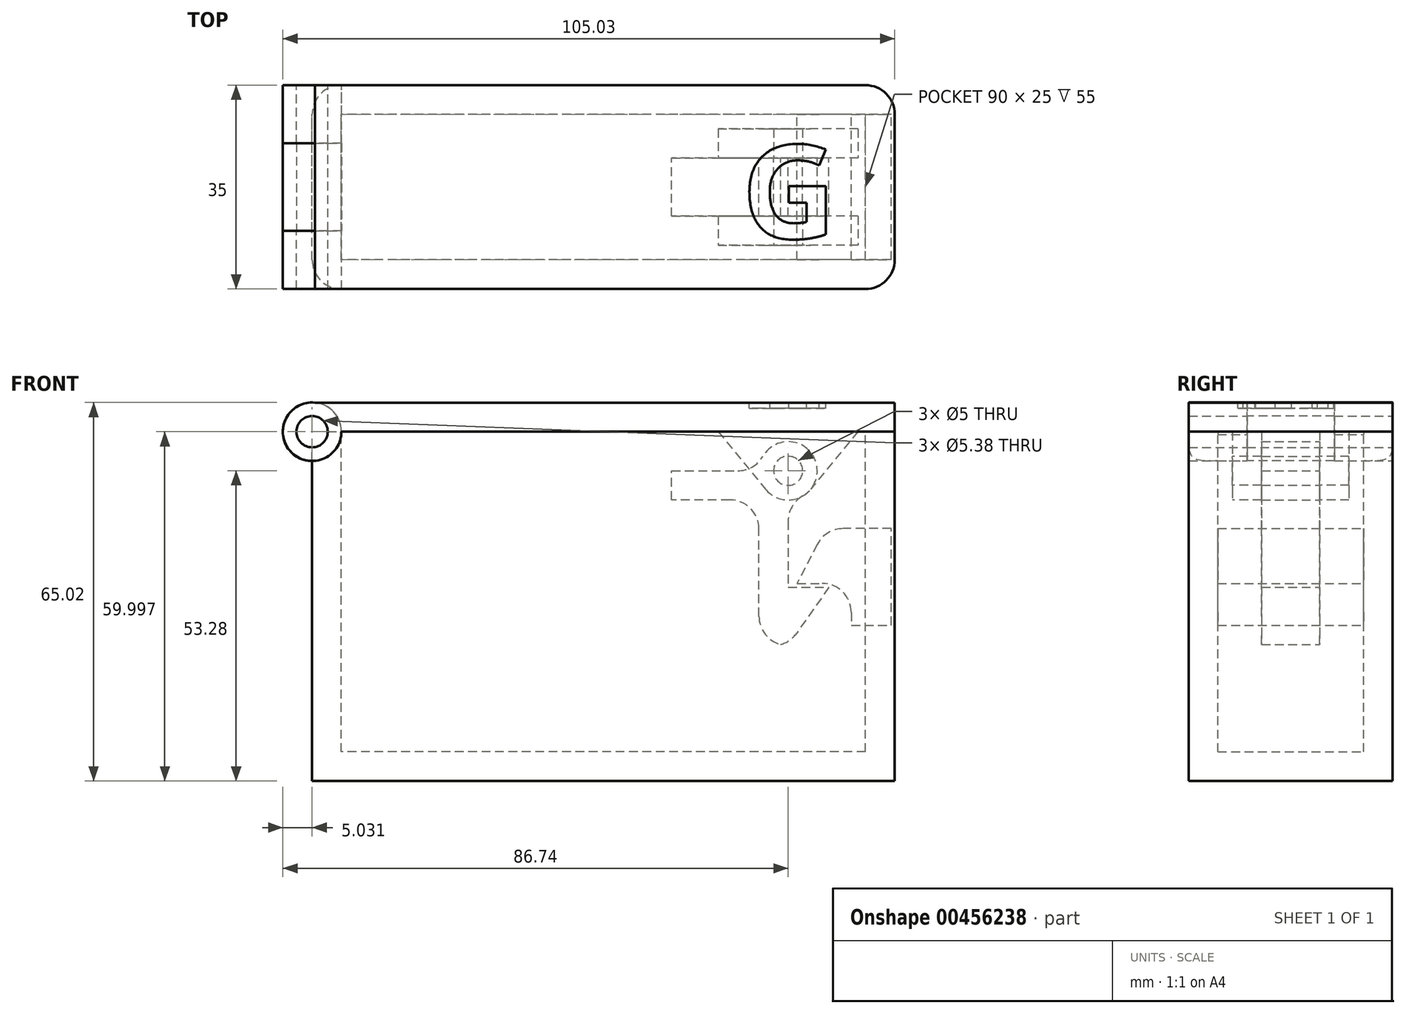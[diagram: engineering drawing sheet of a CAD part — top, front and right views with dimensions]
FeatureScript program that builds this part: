
annotation { "Feature Type Name" : "Feature", "Feature Type Description" : "" }
export const myFeature = defineFeature(function(context is Context, id is Id, definition is map)
    precondition{}
    {
        {
            var Q0;
            Q0=qCreatedBy(makeId("Front.planeOp"),FACE);
            var sketch = newSketch(context, id + "F0", { "sketchPlane" : qUnion([Q0])});
            skLineSegment(sketch, "E0", {"start": v(0, -30) * mm, "end": v(-5, -30) * mm});
            skLineSegment(sketch, "E1", {"start": v(-5, -30) * mm, "end": v(-5, -5) * mm});
            skLineSegment(sketch, "E2", {"start": v(-5, -5) * mm, "end": v(-20, -5) * mm});
            skLineSegment(sketch, "E3", {"start": v(-20, -5) * mm, "end": v(-20, 0) * mm});
            skLineSegment(sketch, "E4", {"start": v(-20, 0) * mm, "end": v(-5, 0) * mm});
            skLineSegment(sketch, "E5", {"start": v(0, -20) * mm, "end": v(7, -20) * mm});
            skLineSegment(sketch, "E6", {"start": v(7, -20) * mm, "end": v(0, -30) * mm});
            skArc(sketch, "E7", {"start": v(0, -5) * mm, "mid": v(3.54, 3.54) * mm, "end": v(-5, 0) * mm});
            skCircle(sketch, "E8", {"center": v(0, 0) * mm, "radius": 2.5 * mm});
            skLineSegment(sketch, "E9.trimOffspring", {"start": v(0, -5) * mm, "end": v(0, -20) * mm});
            skSolve(sketch);
        }
        {
            var Q0;
            Q0=makeQuery(id+"F0.imprint","IMPRINT",FACE,{"disambiguationData":[TD([[makeQuery(id+"F0.imprint","IMPRINT",EDGE,{"derivedFrom":sQuery(id+"F0.wireOp",EDGE,"E0")}),-1.0]])]});
            extrude(context, id + "F1", {"entities" : qUnion([Q0]), "endBound" : BoundingType.SYMMETRIC, "depth" : 10 * mm});
        }
        {
            var Q0;
            Q0=makeQuery(id+"F1.opExtrude","SWEPT_EDGE",EDGE,{"disambiguationData":[OSD([sQuery(id+"F0.wireOp",EDGE,"E1"),sQuery(id+"F0.wireOp",EDGE,"E2")])]});
            var Q1;
            Q1=makeQuery(id+"F1.opExtrude","SWEPT_EDGE",EDGE,{"disambiguationData":[OSD([sQuery(id+"F0.wireOp",EDGE,"E4"),sQuery(id+"F0.wireOp",EDGE,"E7")])]});
            var Q2;
            Q2=makeQuery(id+"F1.opExtrude","SWEPT_EDGE",EDGE,{"disambiguationData":[OSD([sQuery(id+"F0.wireOp",EDGE,"E7"),sQuery(id+"F0.wireOp",EDGE,"E9.trimOffspring")])]});
            var Q3;
            Q3=makeQuery(id+"F1.opExtrude","SWEPT_EDGE",EDGE,{"disambiguationData":[OSD([sQuery(id+"F0.wireOp",EDGE,"E0"),sQuery(id+"F0.wireOp",EDGE,"E6")])]});
            var Q4;
            Q4=makeQuery(id+"F1.opExtrude","SWEPT_EDGE",EDGE,{"disambiguationData":[OSD([sQuery(id+"F0.wireOp",EDGE,"E0"),sQuery(id+"F0.wireOp",EDGE,"E1")])]});
            fillet(context, id + "F2", {"entities" : qUnion([Q0, Q1, Q2, Q3, Q4]), "radius" : 5 * mm, "tangentPropagation" : true, "allowEdgeOverflow" : false});
        }
        {
            var Q0;
            Q0=makeQuery(id+"F1.opExtrude","CAP_FACE",FACE,{"disambiguationData":[OSD([sQuery(id+"F0.wireOp",EDGE,"E0"),sQuery(id+"F0.wireOp",EDGE,"E1"),sQuery(id+"F0.wireOp",EDGE,"E2"),sQuery(id+"F0.wireOp",EDGE,"E3"),sQuery(id+"F0.wireOp",EDGE,"E4"),sQuery(id+"F0.wireOp",EDGE,"E5"),sQuery(id+"F0.wireOp",EDGE,"E6"),sQuery(id+"F0.wireOp",EDGE,"E7"),sQuery(id+"F0.wireOp",EDGE,"E8"),sQuery(id+"F0.wireOp",EDGE,"E9.trimOffspring")])],"isStart":true});
            var sketch = newSketch(context, id + "F3", { "sketchPlane" : qUnion([Q0])});
            skCircle(sketch, "E10.0", {"center": v(0, 0) * mm, "radius": 2.5 * mm});
            skArc(sketch, "E11", {"start": v(-3.86, -3.18) * mm, "mid": v(0, -5) * mm, "end": v(3.86, -3.18) * mm});
            skLineSegment(sketch, "E12", {"start": v(-12.02, 6.72) * mm, "end": v(-3.86, -3.18) * mm});
            skLineSegment(sketch, "E13.MirrorCS", {"start": v(12.02, 6.72) * mm, "end": v(3.86, -3.18) * mm});
            skLineSegment(sketch, "E14", {"start": v(-12.02, 6.72) * mm, "end": v(12.02, 6.72) * mm});
            skSolve(sketch);
        }
        {
            var Q0;
            {var subQ5=sQuery(id+"F3.wireOp",EDGE,"E12");Q0=makeQuery(id+"F3.imprint","IMPRINT",FACE,{"disambiguationData":[TD([[makeQuery(id+"F3.imprint","IMPRINT",EDGE,{"derivedFrom":subQ5}),1.0]])]});}
            var Q1;
            Q1=makeQuery(id+"F3.imprint","IMPRINT",FACE,{"disambiguationData":[TD([[makeQuery(id+"F3.imprint","IMPRINT",EDGE,{"derivedFrom":sQuery(id+"F3.wireOp",EDGE,"E10.0")}),1.0]])]});
            extrude(context, id + "F4", {"entities" : qUnion([Q0, Q1]), "depth" : 5 * mm});
        }
        {
            var Q0;
            Q0=makeQuery(id+"F4.opExtrude","SWEPT_BODY",BODY,{"disambiguationData":[OSD([sQuery(id+"F3.wireOp",EDGE,"E10.0"),sQuery(id+"F3.wireOp",EDGE,"E11"),sQuery(id+"F3.wireOp",EDGE,"E12"),sQuery(id+"F3.wireOp",EDGE,"E13.MirrorCS"),sQuery(id+"F3.wireOp",EDGE,"E14")])]});
            transform(context, id + "F5", {"entities" : qUnion([Q0]), "transformType" : TransformType.TRANSLATION_3D, "dx" : 0 * mm, "dy" : -15 * mm, "dz" : 0 * mm, "makeCopy" : true});
        }
        {
            var Q0;
            Q0=makeQuery(id+"F4.opExtrude","SWEPT_FACE",FACE,{"disambiguationData":[OSD([sQuery(id+"F3.wireOp",EDGE,"E14")])]});
            var sketch = newSketch(context, id + "F6", { "sketchPlane" : qUnion([Q0])});
            skLineSegment(sketch, "E15.bottom", {"start": v(18.3, -17.5) * mm, "end": v(-81.7, -17.5) * mm});
            skLineSegment(sketch, "E15.top", {"start": v(18.3, 17.5) * mm, "end": v(-81.7, 17.5) * mm});
            skLineSegment(sketch, "E15.left", {"start": v(18.3, -17.5) * mm, "end": v(18.3, 17.5) * mm});
            skLineSegment(sketch, "E15.right", {"start": v(-81.7, -17.5) * mm, "end": v(-81.7, 17.5) * mm});
            skPoint(sketch, "E15.middle", {"position": v(-31.7, 0) * mm});
            skSolve(sketch);
        }
        {
            var Q0;
            Q0=makeQuery(id+"F6.imprint","IMPRINT",FACE,{"disambiguationData":[TD([[makeQuery(id+"F6.imprint","IMPRINT",EDGE,{"derivedFrom":sQuery(id+"F6.wireOp",EDGE,"E15.bottom")}),-1.0]])]});
            var Q1;
            {var subQ0=sQuery(id+"F3.wireOp",EDGE,"E14");Q1=makeQuery(id+"F6.imprint","IMPRINT",FACE,{"disambiguationData":[TD([[makeQuery(id+"F6.imprint","IMPRINT",EDGE,{"derivedFrom":makeQuery(id+"F4.opExtrude","CAP_EDGE",EDGE,{"disambiguationData":[OSD([subQ0])],"isStart":true})}),-1.0]])]});}
            extrude(context, id + "F7", {"entities" : qUnion([Q0, Q1]), "depth" : 5 * mm});
        }
        {
            var Q0;
            Q0=makeQuery(id+"F7.opExtrude","CAP_FACE",FACE,{"disambiguationData":[OSD([sQuery(id+"F6.wireOp",EDGE,"E15.bottom"),sQuery(id+"F6.wireOp",EDGE,"E15.top"),sQuery(id+"F6.wireOp",EDGE,"E15.left"),sQuery(id+"F6.wireOp",EDGE,"E15.right")])],"isStart":true});
            var sketch = newSketch(context, id + "F8", { "sketchPlane" : qUnion([Q0])});
            skLineSegment(sketch, "E16.0.0", {"start": v(18.3, -17.5) * mm, "end": v(18.3, 17.5) * mm});
            skLineSegment(sketch, "E16.0.1", {"start": v(18.3, 17.5) * mm, "end": v(-81.7, 17.5) * mm});
            skLineSegment(sketch, "E16.0.2", {"start": v(-81.7, 17.5) * mm, "end": v(-81.7, -17.5) * mm});
            skLineSegment(sketch, "E16.0.3", {"start": v(-81.7, -17.5) * mm, "end": v(18.3, -17.5) * mm});
            skSolve(sketch);
        }
        {
            var Q0;
            Q0=makeQuery(id+"F8.imprint","IMPRINT",FACE,{"disambiguationData":[TD([[makeQuery(id+"F8.imprint","IMPRINT",EDGE,{"derivedFrom":sQuery(id+"F8.wireOp",EDGE,"E16.0.0")}),-1.0]])]});
            extrude(context, id + "F9", {"entities" : qUnion([Q0]), "depth" : 60 * mm});
        }
        {
            var Q0;
            Q0=makeQuery(id+"F9.opExtrude","CAP_FACE",FACE,{"disambiguationData":[OSD([sQuery(id+"F8.wireOp",EDGE,"E16.0.0"),sQuery(id+"F8.wireOp",EDGE,"E16.0.1"),sQuery(id+"F8.wireOp",EDGE,"E16.0.2"),sQuery(id+"F8.wireOp",EDGE,"E16.0.3")])],"isStart":true});
            shell(context, id + "F10", {"entities" : qUnion([Q0]), "thickness" : 5 * mm});
        }
        {
            var Q0;
            Q0=makeQuery(id+"F9.opExtrude","SWEPT_FACE",FACE,{"disambiguationData":[OSD([sQuery(id+"F8.wireOp",EDGE,"E16.0.3")])]});
            var sketch = newSketch(context, id + "F11", { "sketchPlane" : qUnion([Q0])});
            skCircle(sketch, "E17", {"center": v(81.7, 6.72) * mm, "radius": 2.69 * mm});
            skCircle(sketch, "E18", {"center": v(81.7, 6.72) * mm, "radius": 5.03 * mm});
            skSolve(sketch);
        }
        {
            var Q0;
            {var subQ0=sQuery(id+"F11.wireOp",EDGE,"E17");var subQ1=sQuery(id+"F8.wireOp",EDGE,"E16.0.3");var subQ4=makeQuery(id+"F9.opExtrude","CAP_EDGE",EDGE,{"disambiguationData":[OSD([subQ1])],"isStart":true});var subQ5=makeQuery(id+"F11.imprint","INTERSECT",VERTEX,{"derivedFrom":[subQ4,subQ0]});Q0=makeQuery(id+"F11.imprint","IMPRINT",FACE,{"disambiguationData":[TD([[makeQuery(id+"F11.imprint","IMPRINT",EDGE,{"disambiguationData":[TD([[subQ5,1.0]])],"derivedFrom":subQ0}),1.0]])]});}
            var Q1;
            {var subQ0=sQuery(id+"F11.wireOp",EDGE,"E17");var subQ1=sQuery(id+"F8.wireOp",EDGE,"E16.0.3");var subQ4=makeQuery(id+"F9.opExtrude","CAP_EDGE",EDGE,{"disambiguationData":[OSD([subQ1])],"isStart":true});var subQ5=makeQuery(id+"F11.imprint","INTERSECT",VERTEX,{"derivedFrom":[subQ4,subQ0]});Q1=makeQuery(id+"F11.imprint","IMPRINT",FACE,{"disambiguationData":[TD([[makeQuery(id+"F11.imprint","IMPRINT",EDGE,{"disambiguationData":[TD([[subQ5,-1.0]])],"derivedFrom":subQ0}),1.0]])]});}
            extrude(context, id + "F12", {"entities" : qUnion([Q0, Q1]), "operationType" : NewBodyOperationType.REMOVE, "oppositeDirection" : true, "depth" : 37 * mm});
        }
        {
            var Q0;
            {var subQ1=sQuery(id+"F8.wireOp",EDGE,"E16.0.3");var subQ4=makeQuery(id+"F9.opExtrude","CAP_EDGE",EDGE,{"disambiguationData":[OSD([subQ1])],"isStart":true});var subQ6=sQuery(id+"F11.wireOp",EDGE,"E18");var subQ8=makeQuery(id+"F11.imprint","INTERSECT",VERTEX,{"derivedFrom":[subQ4,subQ6]});Q0=makeQuery(id+"F11.imprint","IMPRINT",FACE,{"disambiguationData":[TD([[makeQuery(id+"F11.imprint","IMPRINT",EDGE,{"disambiguationData":[TD([[subQ8,-1.0]])],"derivedFrom":subQ4}),-1.0]])]});}
            var Q1;
            {var subQ1=sQuery(id+"F8.wireOp",EDGE,"E16.0.3");var subQ4=makeQuery(id+"F9.opExtrude","CAP_EDGE",EDGE,{"disambiguationData":[OSD([subQ1])],"isStart":true});var subQ6=sQuery(id+"F11.wireOp",EDGE,"E18");var subQ7=makeQuery(id+"F11.imprint","INTERSECT",VERTEX,{"derivedFrom":[subQ4,subQ6]});Q1=makeQuery(id+"F11.imprint","IMPRINT",FACE,{"disambiguationData":[TD([[makeQuery(id+"F11.imprint","IMPRINT",EDGE,{"disambiguationData":[TD([[subQ7,-1.0]])],"derivedFrom":subQ4}),1.0]])]});}
            extrude(context, id + "F13", {"entities" : qUnion([Q0, Q1]), "oppositeDirection" : true, "depth" : 10 * mm});
        }
        {
            var Q0;
            Q0=makeQuery(id+"F13.opExtrude","SWEPT_BODY",BODY,{"disambiguationData":[OSD([sQuery(id+"F11.wireOp",EDGE,"E17"),sQuery(id+"F11.wireOp",EDGE,"E18")])]});
            transform(context, id + "F14", {"entities" : qUnion([Q0]), "transformType" : TransformType.TRANSLATION_3D, "dx" : 0 * mm, "dy" : -25 * mm, "dz" : 0 * mm, "makeCopy" : true});
        }
        {
            var Q0;
            Q0=makeQuery(id+"F13.opExtrude","SWEPT_BODY",BODY,{"disambiguationData":[OSD([sQuery(id+"F11.wireOp",EDGE,"E17"),sQuery(id+"F11.wireOp",EDGE,"E18")])]});
            var Q1;
            Q1=makeQuery(id+"F14.opPattern","COPY",BODY,{"derivedFrom":makeQuery(id+"F13.opExtrude","SWEPT_BODY",BODY,{"disambiguationData":[OSD([sQuery(id+"F11.wireOp",EDGE,"E17"),sQuery(id+"F11.wireOp",EDGE,"E18")])]}),"instanceName":"1"});
            var Q2;
            Q2=makeQuery(id+"F9.opExtrude","SWEPT_BODY",BODY,{"disambiguationData":[OSD([sQuery(id+"F8.wireOp",EDGE,"E16.0.0"),sQuery(id+"F8.wireOp",EDGE,"E16.0.1"),sQuery(id+"F8.wireOp",EDGE,"E16.0.2"),sQuery(id+"F8.wireOp",EDGE,"E16.0.3")])]});
            booleanBodies(context, id + "F15", {"operationType" : BooleanOperationType.SUBTRACTION, "tools" : qUnion([Q0, Q1]), "targets" : qUnion([Q2]), "keepTools" : true});
        }
        {
            var Q0;
            Q0=makeQuery(id+"F14.opPattern","COPY",BODY,{"derivedFrom":makeQuery(id+"F13.opExtrude","SWEPT_BODY",BODY,{"disambiguationData":[OSD([sQuery(id+"F11.wireOp",EDGE,"E17"),sQuery(id+"F11.wireOp",EDGE,"E18")])]}),"instanceName":"1"});
            var Q1;
            Q1=makeQuery(id+"F13.opExtrude","SWEPT_BODY",BODY,{"disambiguationData":[OSD([sQuery(id+"F11.wireOp",EDGE,"E17"),sQuery(id+"F11.wireOp",EDGE,"E18")])]});
            var Q2;
            Q2=makeQuery(id+"F7.opExtrude","SWEPT_BODY",BODY,{"disambiguationData":[OSD([sQuery(id+"F6.wireOp",EDGE,"E15.bottom"),sQuery(id+"F6.wireOp",EDGE,"E15.top"),sQuery(id+"F6.wireOp",EDGE,"E15.left"),sQuery(id+"F6.wireOp",EDGE,"E15.right")])]});
            booleanBodies(context, id + "F16", {"operationType" : BooleanOperationType.UNION, "tools" : qUnion([Q0, Q1, Q2])});
        }
        {
            var Q0;
            Q0=makeQuery(id+"F14.opPattern","COPY",FACE,{"derivedFrom":makeQuery(id+"F13.opExtrude","CAP_FACE",FACE,{"disambiguationData":[OSD([sQuery(id+"F11.wireOp",EDGE,"E17"),sQuery(id+"F11.wireOp",EDGE,"E18")])],"isStart":true}),"instanceName":"1"});
            var sketch = newSketch(context, id + "F17", { "sketchPlane" : qUnion([Q0])});
            skLineSegment(sketch, "E19.0.0", {"start": v(81.7, 11.72) * mm, "end": v(81.7, 9.4) * mm});
            skArc(sketch, "E19.0.1", {"start": v(81.7, 9.4) * mm, "mid": v(83.6, 4.82) * mm, "end": v(79.02, 6.72) * mm});
            skLineSegment(sketch, "E19.0.2", {"start": v(79.02, 6.72) * mm, "end": v(76.68, 6.72) * mm});
            skArc(sketch, "E19.0.3", {"start": v(76.68, 6.72) * mm, "mid": v(85.44, 3.35) * mm, "end": v(81.2, 11.72) * mm});
            skLineSegment(sketch, "E19.0.4", {"start": v(81.2, 11.72) * mm, "end": v(81.7, 11.72) * mm});
            skCircle(sketch, "E20", {"center": v(81.7, 6.72) * mm, "radius": 2.69 * mm});
            skCircle(sketch, "E21", {"center": v(81.7, 6.72) * mm, "radius": 5.03 * mm});
            skSolve(sketch);
        }
        {
            var Q0;
            Q0 = qSketchRegion(id + "F17", true);
            extrude(context, id + "F18", {"entities" : qUnion([Q0]), "depth" : 15 * mm});
        }
        {
            var Q0;
            Q0=makeQuery(id+"F18.opExtrude","SWEPT_BODY",BODY,{"disambiguationData":[OSD([sQuery(id+"F17.wireOp",EDGE,"E20"),sQuery(id+"F17.wireOp",EDGE,"E21")])]});
            var Q1;
            Q1=makeQuery(id+"F14.opPattern","COPY",BODY,{"derivedFrom":makeQuery(id+"F13.opExtrude","SWEPT_BODY",BODY,{"disambiguationData":[OSD([sQuery(id+"F11.wireOp",EDGE,"E17"),sQuery(id+"F11.wireOp",EDGE,"E18")])]}),"instanceName":"1"});
            booleanBodies(context, id + "F19", {"operationType" : BooleanOperationType.SUBTRACTION, "tools" : qUnion([Q0]), "targets" : qUnion([Q1]), "keepTools" : true});
        }
        {
            var Q0;
            Q0=qCreatedBy(makeId("Front.planeOp"),FACE);
            var sketch = newSketch(context, id + "F20", { "sketchPlane" : qUnion([Q0])});
            skLineSegment(sketch, "E22", {"start": v(1.54, -19.34) * mm, "end": v(10.85, -19.34) * mm});
            skLineSegment(sketch, "E23", {"start": v(10.85, -19.34) * mm, "end": v(10.85, -26.54) * mm});
            skLineSegment(sketch, "E24", {"start": v(10.85, -26.54) * mm, "end": v(17.71, -26.54) * mm});
            skLineSegment(sketch, "E25", {"start": v(17.71, -26.54) * mm, "end": v(17.71, -14.02) * mm});
            skLineSegment(sketch, "E26", {"start": v(17.71, -14.02) * mm, "end": v(17.71, -9.92) * mm});
            skLineSegment(sketch, "E27", {"start": v(17.71, -9.92) * mm, "end": v(6.41, -9.92) * mm});
            skLineSegment(sketch, "E28", {"start": v(6.41, -9.92) * mm, "end": v(1.54, -19.34) * mm});
            skSolve(sketch);
        }
        {
            var Q0;
            Q0 = qSketchRegion(id + "F20", true);
            extrude(context, id + "F21", {"entities" : qUnion([Q0]), "endBound" : BoundingType.SYMMETRIC, "depth" : 25 * mm});
        }
        {
            var Q0;
            Q0=makeQuery(id+"F21.opExtrude","SWEPT_EDGE",EDGE,{"disambiguationData":[OSD([sQuery(id+"F20.wireOp",EDGE,"E27"),sQuery(id+"F20.wireOp",EDGE,"E28")])]});
            var Q1;
            Q1=makeQuery(id+"F21.opExtrude","SWEPT_EDGE",EDGE,{"disambiguationData":[OSD([sQuery(id+"F20.wireOp",EDGE,"E22"),sQuery(id+"F20.wireOp",EDGE,"E23")])]});
            fillet(context, id + "F22", {"entities" : qUnion([Q0, Q1]), "radius" : 5 * mm, "tangentPropagation" : true, "allowEdgeOverflow" : false});
        }
        {
            var Q0;
            Q0=makeQuery(id+"F7.opExtrude","SWEPT_EDGE",EDGE,{"disambiguationData":[OSD([sQuery(id+"F6.wireOp",EDGE,"E15.top"),sQuery(id+"F6.wireOp",EDGE,"E15.left")])]});
            var Q1;
            Q1=makeQuery(id+"F7.opExtrude","SWEPT_EDGE",EDGE,{"disambiguationData":[OSD([sQuery(id+"F6.wireOp",EDGE,"E15.bottom"),sQuery(id+"F6.wireOp",EDGE,"E15.left")])]});
            var Q2;
            Q2=makeQuery(id+"F9.opExtrude","SWEPT_EDGE",EDGE,{"disambiguationData":[OSD([sQuery(id+"F8.wireOp",EDGE,"E16.0.0"),sQuery(id+"F8.wireOp",EDGE,"E16.0.3")])]});
            var Q3;
            Q3=makeQuery(id+"F9.opExtrude","SWEPT_EDGE",EDGE,{"disambiguationData":[OSD([sQuery(id+"F8.wireOp",EDGE,"E16.0.0"),sQuery(id+"F8.wireOp",EDGE,"E16.0.1")])]});
            var Q4;
            Q4=makeQuery(id+"F9.opExtrude","SWEPT_EDGE",EDGE,{"disambiguationData":[OSD([sQuery(id+"F8.wireOp",EDGE,"E16.0.1"),sQuery(id+"F8.wireOp",EDGE,"E16.0.2")])]});
            var Q5;
            Q5=makeQuery(id+"F9.opExtrude","SWEPT_EDGE",EDGE,{"disambiguationData":[OSD([sQuery(id+"F8.wireOp",EDGE,"E16.0.2"),sQuery(id+"F8.wireOp",EDGE,"E16.0.3")])]});
            fillet(context, id + "F23", {"entities" : qUnion([Q0, Q1, Q2, Q3, Q4, Q5]), "radius" : 5 * mm, "tangentPropagation" : true, "allowEdgeOverflow" : false});
        }
        {
            var Q0;
            Q0=makeQuery(id+"F7.opExtrude","CAP_FACE",FACE,{"disambiguationData":[OSD([sQuery(id+"F6.wireOp",EDGE,"E15.bottom"),sQuery(id+"F6.wireOp",EDGE,"E15.top"),sQuery(id+"F6.wireOp",EDGE,"E15.left"),sQuery(id+"F6.wireOp",EDGE,"E15.right")])],"isStart":false});
            var sketch = newSketch(context, id + "F24", { "sketchPlane" : qUnion([Q0])});
            skText(sketch, "E29", { "text": "G", "fontName": "OpenSans-Bold.ttf"});
            const initialGuessF24  = {"E29": [-0.00795, -0.00883, 1, 0, 0.01615]};
            skSetInitialGuess(sketch, initialGuessF24);
            skSolve(sketch);
        }
        {
            var Q0;
            Q0=makeQuery(id+"F24.imprint","IMPRINT",FACE,{"disambiguationData":[TD([[makeQuery(id+"F24.imprint","IMPRINT",EDGE,{"derivedFrom":sQuery(id+"F24.wireOp",EDGE,"E29.sketch_text.stroke-0")}),-1.0]])]});
            extrude(context, id + "F25", {"entities" : qUnion([Q0]), "operationType" : NewBodyOperationType.REMOVE, "oppositeDirection" : true, "depth" : 1 * mm});
        }
    });
